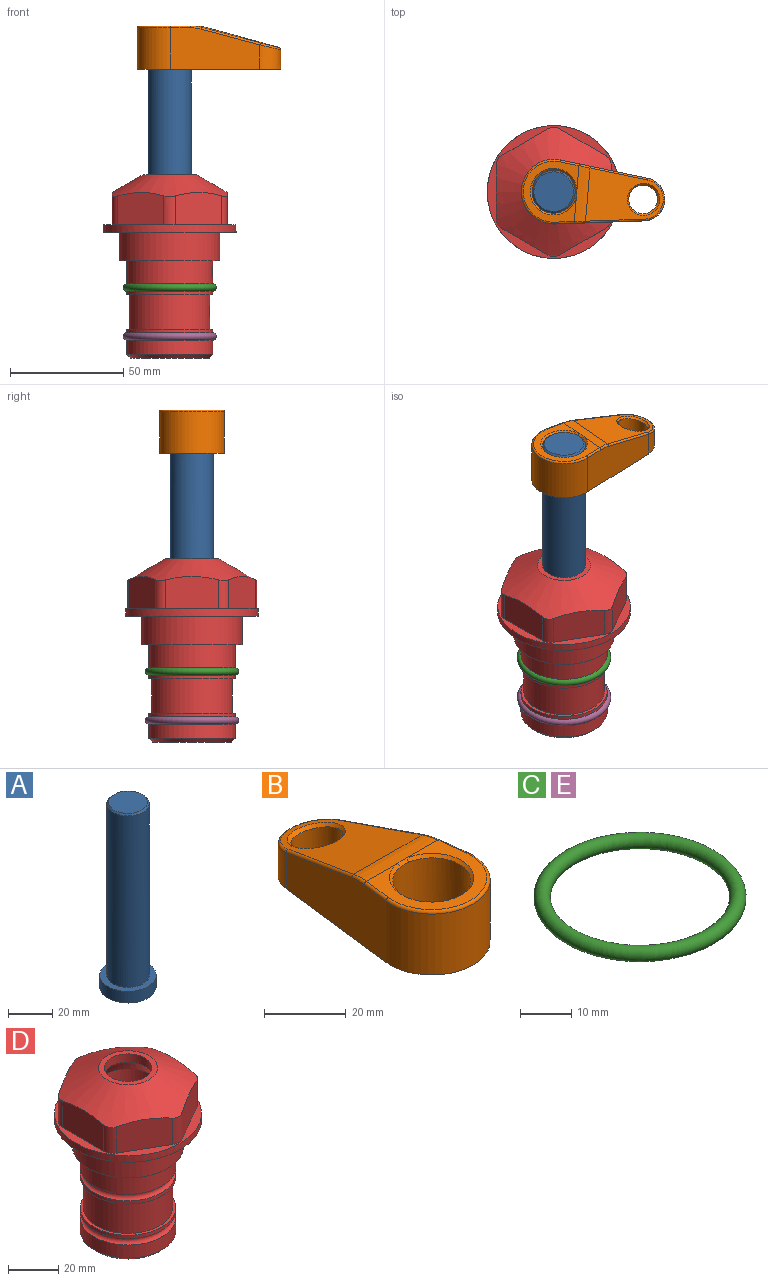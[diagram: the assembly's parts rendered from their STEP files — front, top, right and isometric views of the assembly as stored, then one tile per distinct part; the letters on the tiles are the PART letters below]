
ASSEMBLY  parts=5 mates=4
PART A: 6 faces, bbox 25.4x25.4x101.6 mm
  f0: plane 17.46x17.46mm, normal (0,0,1), area 239.5mm2, adj f5
  f1: plane 25.4x25.4mm, normal (0,0,-1), area 506.7mm2, adj f2
  f2: cylinder r=12.7mm len=25.4mm, axis (0,0,1), area 506.7mm2, adj f1,f3
  f3: plane 25.4x25.4mm, normal (0,0,1), area 221.7mm2, adj f2,f4
  f4: cylinder r=9.53mm len=94.46mm, axis (0,0,1), area 5653mm2, adj f3,f5
  f5: cone r=8.73mm half-angle=45deg, axis (0,0,-1), area 64.4mm2, adj f0,f4
PART B: 31 faces, bbox 31.7x65.5x19.8 mm
  f0: plane 39.12x18.26mm, normal (0.99,0.12,0), area 612.2mm2, adj f1,f4,f7,f11,f13,f15
  f1: cylinder r=9.53mm len=18.91mm, axis (0,0,-1), area 296.1mm2, adj f0,f2,f7,f17
  f2: plane 39.12x18.26mm, normal (-0.99,0.12,0), area 612.2mm2, adj f1,f4,f7,f12,f14,f16
  f3: cylinder r=6.35mm len=12.7mm, axis (0,0,-1), area 362.4mm2, adj f7,f18
  f4: cylinder r=14.29mm len=28.58mm, axis (0,0,-1), area 882.2mm2, adj f0,f2,f7,f10
  f5: cylinder r=9.53mm len=19.05mm, axis (0,0,-1), area 1092.6mm2, adj f7,f19,f20
  f6: plane 26.99x23.69mm, normal (0,0,1), area 216.2mm2, adj f9,f10,f11,f12,f19
  f7: plane 63.5x28.58mm, normal (0,0,-1), area 661.8mm2, adj f0,f1,f2,f3,f4,f5,f22,f23
  f8: plane 33.52x23.6mm, normal (0,0.26,0.97), area 486mm2, adj f9,f15,f16,f17,f18
  f9: cylinder r=19.05mm len=24.72mm, axis (1,0,0), area 120.4mm2, adj f6,f8,f13,f14,f20
  f10: torus R=13.49mm, axis (0,0,1), area 59mm2, adj f4,f6,f11,f12
  f11: cylinder r=0.79mm len=8.67mm, axis (0.12,-0.99,0), area 10.8mm2, adj f0,f6,f10,f13
  f12: cylinder r=0.79mm len=8.67mm, axis (0.12,0.99,0), area 10.8mm2, adj f2,f6,f10,f14
  f13: bspline ~4.95x1.42mm, area 6.1mm2, adj f0,f9,f11,f15
  f14: bspline ~4.95x1.42mm, area 6.1mm2, adj f2,f9,f12,f16
  f15: cylinder r=0.79mm len=25.95mm, axis (0.12,-0.96,0.26), area 32.9mm2, adj f0,f8,f13,f17
  f16: cylinder r=0.79mm len=25.95mm, axis (0.12,0.96,-0.26), area 32.9mm2, adj f2,f8,f14,f17
  f17: bspline ~18.91x8.38mm, area 30mm2, adj f1,f8,f15,f16
  f18: bspline ~14.29x14.29mm, area 48.3mm2, adj f3,f8
  f19: cone r=9.53mm half-angle=45deg, axis (0,0,1), area 66.5mm2, adj f5,f6,f20
  f20: bspline ~3.22x0.96mm, area 3.5mm2, adj f5,f9,f19
  f21: plane 2.75x2.72mm, normal (0,0,-1), area 2.9mm2, adj f23,f25,f28
  f22: plane 23.05x15.88mm, normal (-0.99,-0.12,0), area 323.6mm2, adj f7,f25,f26,f27,f28,f29
  f23: plane 23.05x15.88mm, normal (0.99,-0.12,0), area 323.6mm2, adj f7,f21,f25,f27,f28,f30
  f24: cylinder r=9.53mm len=10.69mm, axis (0,0,-1), area 114.7mm2, adj f7,f27,f29,f30
  f25: cylinder r=12.7mm len=20.59mm, axis (0,0,-1), area 381.1mm2, adj f7,f21,f22,f23,f26,f28
  f26: plane 2.75x2.72mm, normal (0,0,-1), area 2.9mm2, adj f22,f25,f28
  f27: plane 19.72x18.37mm, normal (0,-0.26,-0.97), area 291.8mm2, adj f22,f23,f24,f28,f29,f30
  f28: cylinder r=15.88mm len=19.92mm, axis (1,0,0), area 54.8mm2, adj f21,f22,f23,f25,f26,f27
  f29: cylinder r=1.59mm len=11mm, axis (0,0,-1), area 34.7mm2, adj f7,f22,f24,f27
  f30: cylinder r=1.59mm len=11mm, axis (0,0,-1), area 34.7mm2, adj f7,f23,f24,f27
PART C: 1 faces, bbox 44.7x44.7x3.2 mm
  f0: torus R=19.05mm, axis (0,0,1), area 1193.9mm2
PART D: 36 faces, bbox 58.7x58.7x81 mm
  f0: cylinder r=17.78mm len=35.56mm, axis (0,0,1), area 1670.8mm2, adj f23,f24,f31
  f1: cylinder r=19.05mm len=38.1mm, axis (0,0,1), area 1191.9mm2, adj f26,f27,f30
  f2: plane 58.66x58.66mm, normal (0,0,-1), area 1150.6mm2, adj f3,f28
  f3: cylinder r=29.33mm len=58.66mm, axis (0,0,-1), area 585.1mm2, adj f2,f4
  f4: plane 58.66x58.66mm, normal (0,0,1), area 475.9mm2, adj f3,f5,f6,f7,f8,f9,f10,f11
  f5: plane 20.32x14.34mm, normal (-0.5,0.87,0), area 324.4mm2, adj f4,f15,f16,f17
  f6: plane 20.32x14.34mm, normal (0.5,0.87,0), area 324.4mm2, adj f4,f14,f15,f17
  f7: plane 23.48x14.34mm, normal (1,0,0), area 324.4mm2, adj f4,f13,f14,f17
  f8: plane 20.32x14.34mm, normal (0.5,-0.87,0), area 324.4mm2, adj f4,f12,f13,f17
  f9: plane 20.32x14.34mm, normal (-0.5,-0.87,0), area 324.4mm2, adj f4,f11,f12,f17
  f10: plane 23.48x14.34mm, normal (-1,0,0), area 324.4mm2, adj f4,f11,f16,f17
  f11: cylinder r=5.08mm len=12.85mm, axis (0,0,-1), area 67.2mm2, adj f4,f9,f10,f17
  f12: cylinder r=5.08mm len=12.85mm, axis (0,0,-1), area 67.2mm2, adj f4,f8,f9,f17
  f13: cylinder r=5.08mm len=12.85mm, axis (0,0,-1), area 67.2mm2, adj f4,f7,f8,f17
  f14: cylinder r=5.08mm len=12.85mm, axis (0,0,-1), area 67.2mm2, adj f4,f6,f7,f17
  f15: cylinder r=5.08mm len=12.85mm, axis (0,0,-1), area 67.2mm2, adj f4,f5,f6,f17
  f16: cylinder r=5.08mm len=12.85mm, axis (0,0,-1), area 67.2mm2, adj f4,f5,f10,f17
  f17: cone r=11.73mm half-angle=60deg, axis (0,0,-1), area 2071.8mm2, adj f5,f6,f7,f8,f9,f10,f11,f12
  f18: plane 23.46x23.46mm, normal (0,0,1), area 147.4mm2, adj f17,f35
  f19: plane 34.93x34.93mm, normal (0,0,-1), area 958mm2, adj f29
  f20: cylinder r=19.05mm len=38.1mm, axis (0,0,1), area 760.1mm2, adj f21,f29
  f21: torus R=19.05mm, axis (0,0,1), area 565.3mm2, adj f20,f22
  f22: cylinder r=19.05mm len=38.1mm, axis (0,0,1), area 190mm2, adj f21,f23
  f23: plane 38.1x38.1mm, normal (0,0,1), area 146.9mm2, adj f0,f22
  f24: plane 38.1x38.1mm, normal (0,0,-1), area 146.9mm2, adj f0,f25
  f25: cylinder r=19.05mm len=38.1mm, axis (0,0,1), area 190mm2, adj f24,f26
  f26: torus R=19.05mm, axis (0,0,1), area 565.3mm2, adj f1,f25
  f27: plane 44.45x44.45mm, normal (0,0,-1), area 411.7mm2, adj f1,f28
  f28: cylinder r=22.23mm len=44.45mm, axis (0,0,1), area 1773.5mm2, adj f2,f27
  f29: cone r=19.05mm half-angle=45deg, axis (0,0,1), area 257.5mm2, adj f19,f20
  f30: cylinder r=3.17mm len=6.75mm, axis (-1,0,0), area 128mm2, adj f1,f33
  f31: cylinder r=3.17mm len=6.35mm, axis (-1,0,0), area 102.5mm2, adj f0,f33
  f32: plane 25.4x25.4mm, normal (0,0,1), area 506.7mm2, adj f33
  f33: cylinder r=12.7mm len=66.42mm, axis (0,0,-1), area 5236.2mm2, adj f30,f31,f32,f34
  f34: cone r=9.53mm half-angle=30deg, axis (0,0,-1), area 443.4mm2, adj f33,f35
  f35: cylinder r=9.53mm len=19.05mm, axis (0,0,-1), area 240.9mm2, adj f18,f34
PART E: same geometry as C
PLACE A rot(axis=(0,0,-1),94.9deg) t=(0,0,27.55)mm
PLACE B rot(axis=(0,0,-1),94.9deg) t=(0,0,27.55)mm
PLACE C at identity
PLACE D at identity fixed
PLACE E t=(0,0,-21.59)mm
MATE cylindrical A.f2 <-> D.f0  axis (0,0,-1) through (0,0,-10.55)mm
MATE fastened E.f0 <-> D.f0  axis (0,0,1) through (0,0,-46.1)mm
MATE fastened A.f2 <-> B.f4  axis (0,0,1) through (0,0,91.05)mm
MATE fastened D.f0 <-> C.f0  axis (0,0,1) through (0,0,-24.51)mm
